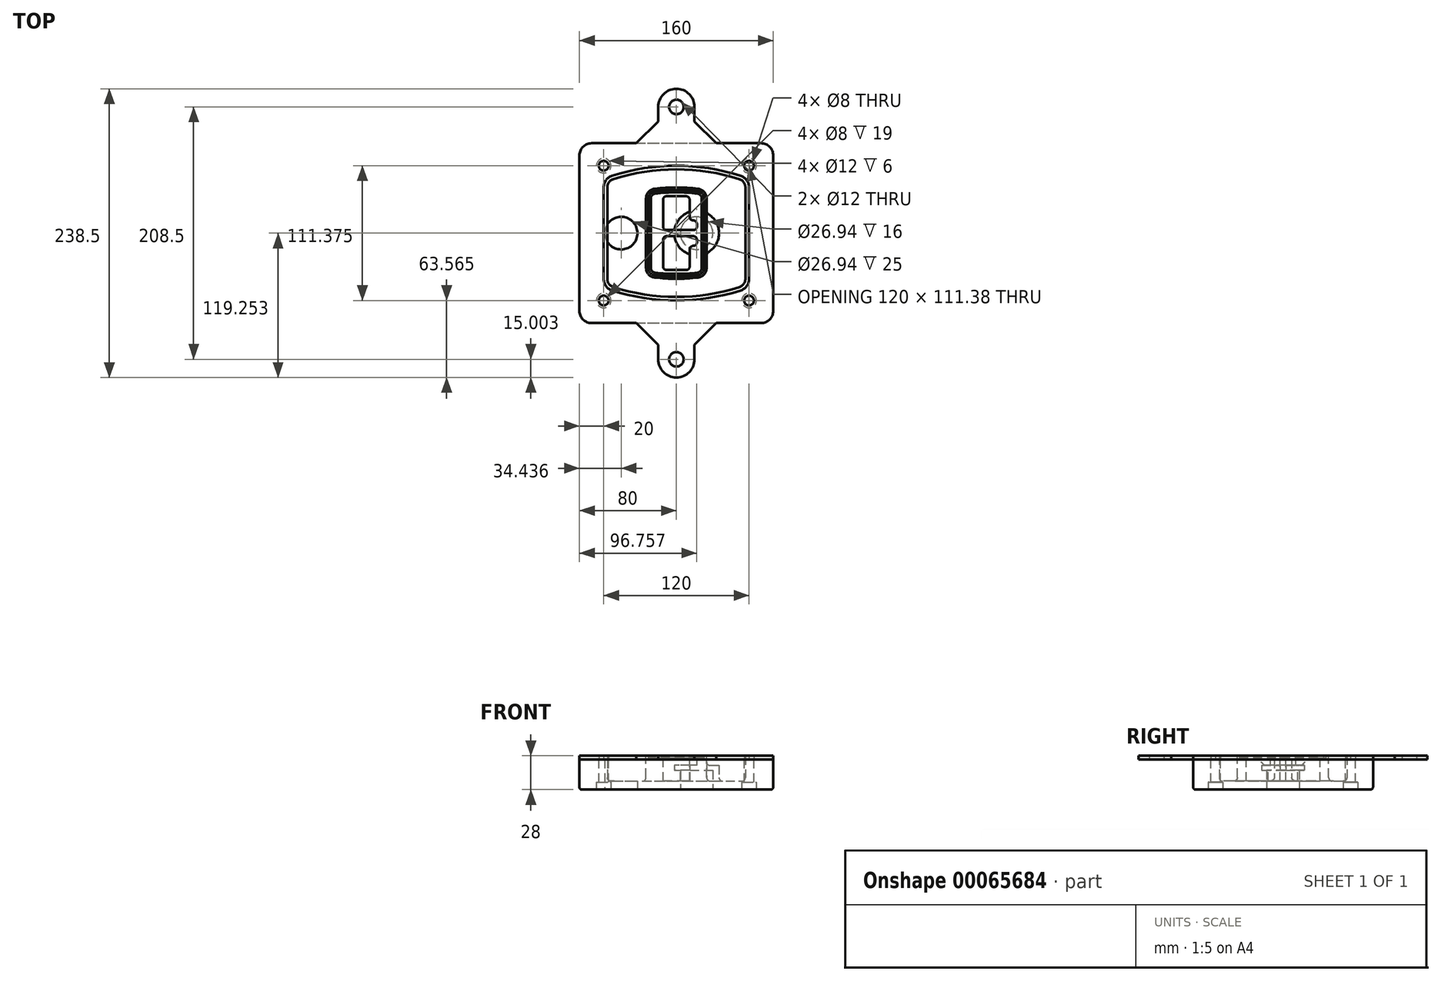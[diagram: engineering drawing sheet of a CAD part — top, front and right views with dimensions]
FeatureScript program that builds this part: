
annotation { "Feature Type Name" : "Feature", "Feature Type Description" : "" }
export const myFeature = defineFeature(function(context is Context, id is Id, definition is map)
    precondition{}
    {
        {
            var Q0;
            Q0=qCreatedBy(makeId("Top.planeOp"),FACE);
            var sketch = newSketch(context, id + "F0", { "sketchPlane" : qUnion([Q0])});
            skPoint(sketch, "E0.rect.middle", {"position": v(0, 0) * mm});
            skLineSegment(sketch, "E1.bottom", {"start": v(24.05, 28.38) * mm, "end": v(164.05, 28.38) * mm});
            skLineSegment(sketch, "E1.top", {"start": v(24.05, 176.88) * mm, "end": v(164.05, 176.88) * mm});
            skLineSegment(sketch, "E1.left", {"start": v(14.05, 38.38) * mm, "end": v(14.05, 166.88) * mm});
            skLineSegment(sketch, "E1.right", {"start": v(174.05, 38.38) * mm, "end": v(174.05, 166.88) * mm});
            skLineSegment(sketch, "E2", {"start": v(14.05, 176.88) * mm, "end": v(174.05, 28.38) * mm, "construction": true});
            skLineSegment(sketch, "E3", {"start": v(174.05, 176.88) * mm, "end": v(14.05, 28.38) * mm, "construction": true});
            skCircle(sketch, "E4", {"center": v(34.05, 158.32) * mm, "radius": 4 * mm});
            skCircle(sketch, "E5", {"center": v(154.05, 158.32) * mm, "radius": 4 * mm});
            skCircle(sketch, "E6", {"center": v(154.05, 46.95) * mm, "radius": 4 * mm});
            skCircle(sketch, "E7", {"center": v(34.05, 46.95) * mm, "radius": 4 * mm});
            skLineSegment(sketch, "E8", {"start": v(34.05, 158.32) * mm, "end": v(154.05, 158.32) * mm, "construction": true});
            skLineSegment(sketch, "E9", {"start": v(154.05, 158.32) * mm, "end": v(154.05, 46.95) * mm, "construction": true});
            skLineSegment(sketch, "E10", {"start": v(154.05, 46.95) * mm, "end": v(34.05, 46.95) * mm, "construction": true});
            skLineSegment(sketch, "E11", {"start": v(34.05, 46.95) * mm, "end": v(34.05, 158.32) * mm, "construction": true});
            skLineSegment(sketch, "E12", {"start": v(34.05, 140.5) * mm, "end": v(34.05, 64.76) * mm});
            skLineSegment(sketch, "E13", {"start": v(154.05, 140.5) * mm, "end": v(154.05, 64.76) * mm});
            skArc(sketch, "E14", {"start": v(147.1, 150.02) * mm, "mid": v(94.05, 158.32) * mm, "end": v(41, 150.02) * mm});
            skArc(sketch, "E15", {"start": v(41, 55.24) * mm, "mid": v(94.05, 46.95) * mm, "end": v(147.1, 55.24) * mm});
            skLineSegment(sketch, "E16", {"start": v(34.05, 102.63) * mm, "end": v(154.05, 102.63) * mm, "construction": true});
            skPoint(sketch, "E17.visualSharp", {"position": v(34.05, 57.63) * mm});
            skArc(sketch, "E17.filletArc", {"start": v(34.05, 64.76) * mm, "mid": v(35.97, 58.87) * mm, "end": v(41, 55.24) * mm});
            skPoint(sketch, "E18.visualSharp", {"position": v(34.05, 147.63) * mm});
            skArc(sketch, "E18.filletArc", {"start": v(41, 150.02) * mm, "mid": v(35.97, 146.4) * mm, "end": v(34.05, 140.5) * mm});
            skPoint(sketch, "E19.visualSharp", {"position": v(154.05, 147.63) * mm});
            skArc(sketch, "E19.filletArc", {"start": v(154.05, 140.5) * mm, "mid": v(152.13, 146.4) * mm, "end": v(147.1, 150.02) * mm});
            skPoint(sketch, "E20.visualSharp", {"position": v(154.05, 57.63) * mm});
            skArc(sketch, "E20.filletArc", {"start": v(147.1, 55.24) * mm, "mid": v(152.13, 58.87) * mm, "end": v(154.05, 64.76) * mm});
            skPoint(sketch, "E21.visualSharp", {"position": v(14.05, 176.88) * mm});
            skArc(sketch, "E21.filletArc", {"start": v(24.05, 176.88) * mm, "mid": v(16.98, 173.95) * mm, "end": v(14.05, 166.88) * mm});
            skPoint(sketch, "E22.visualSharp", {"position": v(174.05, 176.88) * mm});
            skArc(sketch, "E22.filletArc", {"start": v(174.05, 166.88) * mm, "mid": v(171.12, 173.95) * mm, "end": v(164.05, 176.88) * mm});
            skPoint(sketch, "E23.visualSharp", {"position": v(174.05, 28.38) * mm});
            skArc(sketch, "E23.filletArc", {"start": v(164.05, 28.38) * mm, "mid": v(171.12, 31.31) * mm, "end": v(174.05, 38.38) * mm});
            skPoint(sketch, "E24.visualSharp", {"position": v(14.05, 28.38) * mm});
            skArc(sketch, "E24.filletArc", {"start": v(14.05, 38.38) * mm, "mid": v(16.98, 31.31) * mm, "end": v(24.05, 28.38) * mm});
            skArc(sketch, "E25.0", {"start": v(151.05, 140.5) * mm, "mid": v(149.7, 144.63) * mm, "end": v(146.19, 147.17) * mm});
            skLineSegment(sketch, "E25.1", {"start": v(151.05, 140.5) * mm, "end": v(151.05, 64.76) * mm});
            skArc(sketch, "E25.2", {"start": v(146.19, 58.1) * mm, "mid": v(149.7, 60.64) * mm, "end": v(151.05, 64.76) * mm});
            skArc(sketch, "E25.3", {"start": v(41.91, 58.1) * mm, "mid": v(94.05, 49.95) * mm, "end": v(146.19, 58.1) * mm});
            skArc(sketch, "E25.4", {"start": v(37.05, 64.76) * mm, "mid": v(38.4, 60.64) * mm, "end": v(41.91, 58.1) * mm});
            skArc(sketch, "E25.5", {"start": v(146.19, 147.17) * mm, "mid": v(94.05, 155.32) * mm, "end": v(41.91, 147.17) * mm});
            skLineSegment(sketch, "E25.6", {"start": v(37.05, 140.5) * mm, "end": v(37.05, 64.76) * mm});
            skArc(sketch, "E25.7", {"start": v(41.91, 147.17) * mm, "mid": v(38.4, 144.63) * mm, "end": v(37.05, 140.5) * mm});
            skArc(sketch, "E26.0", {"start": v(39.78, 153.83) * mm, "mid": v(32.74, 148.75) * mm, "end": v(30.05, 140.5) * mm});
            skArc(sketch, "E26.1", {"start": v(148.32, 153.83) * mm, "mid": v(94.05, 162.32) * mm, "end": v(39.78, 153.83) * mm});
            skArc(sketch, "E26.2", {"start": v(158.05, 140.5) * mm, "mid": v(155.36, 148.75) * mm, "end": v(148.32, 153.83) * mm});
            skLineSegment(sketch, "E26.3", {"start": v(158.05, 140.5) * mm, "end": v(158.05, 64.76) * mm});
            skArc(sketch, "E26.4", {"start": v(148.32, 51.43) * mm, "mid": v(155.36, 56.51) * mm, "end": v(158.05, 64.76) * mm});
            skLineSegment(sketch, "E26.5", {"start": v(30.05, 140.5) * mm, "end": v(30.05, 64.76) * mm});
            skArc(sketch, "E26.6", {"start": v(39.78, 51.43) * mm, "mid": v(94.05, 42.95) * mm, "end": v(148.32, 51.43) * mm});
            skArc(sketch, "E26.7", {"start": v(30.05, 64.76) * mm, "mid": v(32.74, 56.51) * mm, "end": v(39.78, 51.43) * mm});
            skSolve(sketch);
        }
        {
            var Q0;
            Q0=makeQuery(id+"F0.imprint","IMPRINT",FACE,{"disambiguationData":[TD([[makeQuery(id+"F0.imprint","IMPRINT",EDGE,{"derivedFrom":sQuery(id+"F0.wireOp",EDGE,"E1.bottom")}),1.0]])]});
            var Q1;
            Q1=makeQuery(id+"F0.imprint","IMPRINT",FACE,{"disambiguationData":[TD([[makeQuery(id+"F0.imprint","IMPRINT",EDGE,{"derivedFrom":sQuery(id+"F0.wireOp",EDGE,"E12")}),1.0]])]});
            var Q2;
            Q2=makeQuery(id+"F0.imprint","IMPRINT",FACE,{"disambiguationData":[TD([[makeQuery(id+"F0.imprint","IMPRINT",EDGE,{"derivedFrom":sQuery(id+"F0.wireOp",EDGE,"E25.0")}),1.0]])]});
            var Q3;
            Q3=makeQuery(id+"F0.imprint","IMPRINT",FACE,{"disambiguationData":[TD([[makeQuery(id+"F0.imprint","IMPRINT",EDGE,{"derivedFrom":sQuery(id+"F0.wireOp",EDGE,"E12")}),-1.0]])]});
            extrude(context, id + "F1", {"entities" : qUnion([Q0, Q1, Q2, Q3]), "oppositeDirection" : true, "depth" : 25 * mm});
        }
        {
            var Q0;
            Q0=makeQuery(id+"F0.imprint","IMPRINT",FACE,{"disambiguationData":[TD([[makeQuery(id+"F0.imprint","IMPRINT",EDGE,{"derivedFrom":sQuery(id+"F0.wireOp",EDGE,"E12")}),1.0]])]});
            extrude(context, id + "F2", {"entities" : qUnion([Q0]), "operationType" : NewBodyOperationType.ADD, "depth" : 3 * mm});
        }
        {
            var Q0;
            Q0=makeQuery(id+"F0.imprint","IMPRINT",FACE,{"disambiguationData":[TD([[makeQuery(id+"F0.imprint","IMPRINT",EDGE,{"derivedFrom":sQuery(id+"F0.wireOp",EDGE,"E25.0")}),1.0]])]});
            extrude(context, id + "F3", {"entities" : qUnion([Q0]), "operationType" : NewBodyOperationType.REMOVE, "oppositeDirection" : true, "depth" : 18 * mm});
        }
        {
            var Q0;
            Q0=makeQuery(id+"F2.opExtrude","CAP_FACE",FACE,{"disambiguationData":[OSD([sQuery(id+"F0.wireOp",EDGE,"E12"),sQuery(id+"F0.wireOp",EDGE,"E13"),sQuery(id+"F0.wireOp",EDGE,"E14"),sQuery(id+"F0.wireOp",EDGE,"E15"),sQuery(id+"F0.wireOp",EDGE,"E17.filletArc"),sQuery(id+"F0.wireOp",EDGE,"E18.filletArc"),sQuery(id+"F0.wireOp",EDGE,"E19.filletArc"),sQuery(id+"F0.wireOp",EDGE,"E20.filletArc"),sQuery(id+"F0.wireOp",EDGE,"E25.0"),sQuery(id+"F0.wireOp",EDGE,"E25.1"),sQuery(id+"F0.wireOp",EDGE,"E25.2"),sQuery(id+"F0.wireOp",EDGE,"E25.3"),sQuery(id+"F0.wireOp",EDGE,"E25.4"),sQuery(id+"F0.wireOp",EDGE,"E25.5"),sQuery(id+"F0.wireOp",EDGE,"E25.6"),sQuery(id+"F0.wireOp",EDGE,"E25.7")])],"isStart":false});
            var sketch = newSketch(context, id + "F4", { "sketchPlane" : qUnion([Q0])});
            skArc(sketch, "E27.0", {"start": v(76.13, 65.98) * mm, "mid": v(94.05, 64.95) * mm, "end": v(111.97, 65.98) * mm});
            skArc(sketch, "E28.0", {"start": v(111.97, 139.29) * mm, "mid": v(94.05, 140.32) * mm, "end": v(76.13, 139.29) * mm});
            skLineSegment(sketch, "E29", {"start": v(69.05, 131.34) * mm, "end": v(69.05, 73.93) * mm});
            skLineSegment(sketch, "E30", {"start": v(119.05, 131.34) * mm, "end": v(119.05, 73.93) * mm});
            skLineSegment(sketch, "E31", {"start": v(69.05, 138.3) * mm, "end": v(119.05, 138.3) * mm, "construction": true});
            skLineSegment(sketch, "E32", {"start": v(69.05, 66.96) * mm, "end": v(119.05, 66.96) * mm, "construction": true});
            skPoint(sketch, "E33.visualSharp", {"position": v(69.05, 138.3) * mm});
            skArc(sketch, "E33.filletArc", {"start": v(76.13, 139.29) * mm, "mid": v(71.08, 136.66) * mm, "end": v(69.05, 131.34) * mm});
            skPoint(sketch, "E34.visualSharp", {"position": v(119.05, 138.3) * mm});
            skArc(sketch, "E34.filletArc", {"start": v(119.05, 131.34) * mm, "mid": v(117.02, 136.66) * mm, "end": v(111.97, 139.29) * mm});
            skPoint(sketch, "E35.visualSharp", {"position": v(119.05, 66.96) * mm});
            skArc(sketch, "E35.filletArc", {"start": v(111.97, 65.98) * mm, "mid": v(117.02, 68.6) * mm, "end": v(119.05, 73.93) * mm});
            skPoint(sketch, "E36.visualSharp", {"position": v(69.05, 66.96) * mm});
            skArc(sketch, "E36.filletArc", {"start": v(69.05, 73.93) * mm, "mid": v(71.08, 68.6) * mm, "end": v(76.13, 65.98) * mm});
            skArc(sketch, "E37.0", {"start": v(146.19, 147.17) * mm, "mid": v(94.05, 155.32) * mm, "end": v(41.91, 147.17) * mm});
            skArc(sketch, "E37.1", {"start": v(41.91, 147.17) * mm, "mid": v(38.4, 144.63) * mm, "end": v(37.05, 140.5) * mm});
            skLineSegment(sketch, "E37.2", {"start": v(37.05, 140.5) * mm, "end": v(37.05, 64.76) * mm});
            skArc(sketch, "E37.3", {"start": v(37.05, 64.76) * mm, "mid": v(38.4, 60.64) * mm, "end": v(41.91, 58.1) * mm});
            skArc(sketch, "E37.4", {"start": v(41.91, 58.1) * mm, "mid": v(94.05, 49.95) * mm, "end": v(146.19, 58.1) * mm});
            skArc(sketch, "E37.5", {"start": v(146.19, 58.1) * mm, "mid": v(149.7, 60.64) * mm, "end": v(151.05, 64.76) * mm});
            skLineSegment(sketch, "E37.6", {"start": v(151.05, 140.5) * mm, "end": v(151.05, 64.76) * mm});
            skArc(sketch, "E37.7", {"start": v(151.05, 140.5) * mm, "mid": v(149.7, 144.63) * mm, "end": v(146.19, 147.17) * mm});
            skLineSegment(sketch, "E38.0", {"start": v(117.05, 131.34) * mm, "end": v(117.05, 73.93) * mm});
            skArc(sketch, "E38.1", {"start": v(111.74, 67.97) * mm, "mid": v(115.53, 69.94) * mm, "end": v(117.05, 73.93) * mm});
            skArc(sketch, "E38.2", {"start": v(76.36, 67.97) * mm, "mid": v(94.05, 66.95) * mm, "end": v(111.74, 67.97) * mm});
            skArc(sketch, "E38.3", {"start": v(71.05, 73.93) * mm, "mid": v(72.57, 69.94) * mm, "end": v(76.36, 67.97) * mm});
            skLineSegment(sketch, "E38.4", {"start": v(71.05, 131.34) * mm, "end": v(71.05, 73.93) * mm});
            skArc(sketch, "E38.5", {"start": v(117.05, 131.34) * mm, "mid": v(115.53, 135.33) * mm, "end": v(111.74, 137.3) * mm});
            skArc(sketch, "E38.6", {"start": v(76.36, 137.3) * mm, "mid": v(72.57, 135.33) * mm, "end": v(71.05, 131.34) * mm});
            skArc(sketch, "E38.7", {"start": v(111.74, 137.3) * mm, "mid": v(94.05, 138.32) * mm, "end": v(76.36, 137.3) * mm});
            skArc(sketch, "E39.0", {"start": v(115.05, 131.34) * mm, "mid": v(114.04, 134) * mm, "end": v(111.51, 135.31) * mm});
            skLineSegment(sketch, "E39.1", {"start": v(115.05, 131.34) * mm, "end": v(115.05, 73.93) * mm});
            skArc(sketch, "E39.2", {"start": v(111.51, 69.95) * mm, "mid": v(114.04, 71.27) * mm, "end": v(115.05, 73.93) * mm});
            skArc(sketch, "E39.3", {"start": v(76.59, 69.95) * mm, "mid": v(94.05, 68.95) * mm, "end": v(111.51, 69.95) * mm});
            skArc(sketch, "E39.4", {"start": v(73.05, 73.93) * mm, "mid": v(74.06, 71.27) * mm, "end": v(76.59, 69.95) * mm});
            skArc(sketch, "E39.5", {"start": v(111.51, 135.31) * mm, "mid": v(94.05, 136.32) * mm, "end": v(76.59, 135.31) * mm});
            skLineSegment(sketch, "E39.6", {"start": v(73.05, 131.34) * mm, "end": v(73.05, 73.93) * mm});
            skArc(sketch, "E39.7", {"start": v(76.59, 135.31) * mm, "mid": v(74.06, 134) * mm, "end": v(73.05, 131.34) * mm});
            skLineSegment(sketch, "E40", {"start": v(69.05, 102.63) * mm, "end": v(119.05, 102.63) * mm, "construction": true});
            skLineSegment(sketch, "E41", {"start": v(83.05, 108.13) * mm, "end": v(83.05, 130.13) * mm});
            skLineSegment(sketch, "E42", {"start": v(86.05, 133.13) * mm, "end": v(102.05, 133.13) * mm});
            skLineSegment(sketch, "E43", {"start": v(105.05, 130.13) * mm, "end": v(105.05, 116.13) * mm});
            skLineSegment(sketch, "E44", {"start": v(108.05, 113.13) * mm, "end": v(108.05, 113.13) * mm});
            skLineSegment(sketch, "E45", {"start": v(111.05, 110.13) * mm, "end": v(111.05, 108.13) * mm});
            skLineSegment(sketch, "E46", {"start": v(108.05, 105.13) * mm, "end": v(86.05, 105.13) * mm});
            skPoint(sketch, "E47.visualSharp", {"position": v(83.05, 133.13) * mm});
            skArc(sketch, "E47.filletArc", {"start": v(86.05, 133.13) * mm, "mid": v(83.93, 132.25) * mm, "end": v(83.05, 130.13) * mm});
            skPoint(sketch, "E48.visualSharp", {"position": v(105.05, 133.13) * mm});
            skArc(sketch, "E48.filletArc", {"start": v(105.05, 130.13) * mm, "mid": v(104.17, 132.25) * mm, "end": v(102.05, 133.13) * mm});
            skPoint(sketch, "E49.visualSharp", {"position": v(105.05, 113.13) * mm});
            skArc(sketch, "E49.filletArc", {"start": v(105.05, 116.13) * mm, "mid": v(105.93, 114.01) * mm, "end": v(108.05, 113.13) * mm});
            skPoint(sketch, "E50.visualSharp", {"position": v(111.05, 113.13) * mm});
            skArc(sketch, "E50.filletArc", {"start": v(111.05, 110.13) * mm, "mid": v(110.17, 112.25) * mm, "end": v(108.05, 113.13) * mm});
            skPoint(sketch, "E51.visualSharp", {"position": v(111.05, 105.13) * mm});
            skArc(sketch, "E51.filletArc", {"start": v(108.05, 105.13) * mm, "mid": v(110.17, 106.01) * mm, "end": v(111.05, 108.13) * mm});
            skPoint(sketch, "E52.visualSharp", {"position": v(83.05, 105.13) * mm});
            skArc(sketch, "E52.filletArc", {"start": v(83.05, 108.13) * mm, "mid": v(83.93, 106.01) * mm, "end": v(86.05, 105.13) * mm});
            skLineSegment(sketch, "E53.0.MirrorCS", {"start": v(108.05, 100.13) * mm, "end": v(86.05, 100.13) * mm});
            skArc(sketch, "E54.0.MirrorCS", {"start": v(83.05, 97.13) * mm, "mid": v(83.93, 99.25) * mm, "end": v(86.05, 100.13) * mm});
            skLineSegment(sketch, "E55.0.MirrorCS", {"start": v(83.05, 97.13) * mm, "end": v(83.05, 75.13) * mm});
            skArc(sketch, "E56.0.MirrorCS", {"start": v(86.05, 72.13) * mm, "mid": v(83.93, 73.01) * mm, "end": v(83.05, 75.13) * mm});
            skLineSegment(sketch, "E57.0.MirrorCS", {"start": v(86.05, 72.13) * mm, "end": v(102.05, 72.13) * mm});
            skArc(sketch, "E58.0.MirrorCS", {"start": v(105.05, 75.13) * mm, "mid": v(104.17, 73.01) * mm, "end": v(102.05, 72.13) * mm});
            skLineSegment(sketch, "E59.0.MirrorCS", {"start": v(105.05, 75.13) * mm, "end": v(105.05, 89.13) * mm});
            skArc(sketch, "E60.0.MirrorCS", {"start": v(105.05, 89.13) * mm, "mid": v(105.93, 91.25) * mm, "end": v(108.05, 92.13) * mm});
            skArc(sketch, "E61.0.MirrorCS", {"start": v(111.05, 95.13) * mm, "mid": v(110.17, 93.01) * mm, "end": v(108.05, 92.13) * mm});
            skLineSegment(sketch, "E62.0.MirrorCS", {"start": v(111.05, 95.13) * mm, "end": v(111.05, 97.13) * mm});
            skArc(sketch, "E63.0.MirrorCS", {"start": v(108.05, 100.13) * mm, "mid": v(110.17, 99.25) * mm, "end": v(111.05, 97.13) * mm});
            skSolve(sketch);
        }
        {
            var Q0;
            Q0=makeQuery(id+"F4.imprint","IMPRINT",FACE,{"disambiguationData":[TD([[makeQuery(id+"F4.imprint","IMPRINT",EDGE,{"derivedFrom":sQuery(id+"F4.wireOp",EDGE,"E27.0")}),1.0]])]});
            var Q1;
            Q1=makeQuery(id+"F4.imprint","IMPRINT",FACE,{"disambiguationData":[TD([[makeQuery(id+"F4.imprint","IMPRINT",EDGE,{"derivedFrom":sQuery(id+"F4.wireOp",EDGE,"E38.0")}),-1.0]])]});
            var Q2;
            Q2=makeQuery(id+"F4.imprint","IMPRINT",FACE,{"disambiguationData":[TD([[makeQuery(id+"F4.imprint","IMPRINT",EDGE,{"derivedFrom":sQuery(id+"F4.wireOp",EDGE,"E39.0")}),1.0]])]});
            extrude(context, id + "F5", {"entities" : qUnion([Q0, Q1, Q2]), "operationType" : NewBodyOperationType.ADD, "endBound" : BoundingType.UP_TO_NEXT, "oppositeDirection" : true, "depth" : 25 * mm});
        }
        {
            var Q0;
            Q0=makeQuery(id+"F4.imprint","IMPRINT",FACE,{"disambiguationData":[TD([[makeQuery(id+"F4.imprint","IMPRINT",EDGE,{"derivedFrom":sQuery(id+"F4.wireOp",EDGE,"E38.0")}),-1.0]])]});
            extrude(context, id + "F6", {"entities" : qUnion([Q0]), "operationType" : NewBodyOperationType.REMOVE, "oppositeDirection" : true, "depth" : 2 * mm});
        }
        {
            var Q0;
            Q0=makeQuery(id+"F1.opExtrude","CAP_FACE",FACE,{"disambiguationData":[OSD([sQuery(id+"F0.wireOp",EDGE,"E1.bottom"),sQuery(id+"F0.wireOp",EDGE,"E1.top"),sQuery(id+"F0.wireOp",EDGE,"E1.left"),sQuery(id+"F0.wireOp",EDGE,"E1.right"),sQuery(id+"F0.wireOp",EDGE,"E4"),sQuery(id+"F0.wireOp",EDGE,"E5"),sQuery(id+"F0.wireOp",EDGE,"E6"),sQuery(id+"F0.wireOp",EDGE,"E7"),sQuery(id+"F0.wireOp",EDGE,"E21.filletArc"),sQuery(id+"F0.wireOp",EDGE,"E22.filletArc"),sQuery(id+"F0.wireOp",EDGE,"E23.filletArc"),sQuery(id+"F0.wireOp",EDGE,"E24.filletArc")])],"isStart":false});
            var sketch = newSketch(context, id + "F7", { "sketchPlane" : qUnion([Q0])});
            skCircle(sketch, "E64", {"center": v(110.8, -102.63) * mm, "radius": 13.47 * mm});
            skCircle(sketch, "E65", {"center": v(48.49, -102.63) * mm, "radius": 13.47 * mm});
            skLineSegment(sketch, "E66", {"start": v(174.05, -102.63) * mm, "end": v(14.05, -102.63) * mm});
            skCircle(sketch, "E67", {"center": v(110.8, -102.63) * mm, "radius": 18.47 * mm});
            skCircle(sketch, "E68", {"center": v(154.05, -158.32) * mm, "radius": 6 * mm});
            skCircle(sketch, "E69", {"center": v(34.05, -158.32) * mm, "radius": 6 * mm});
            skCircle(sketch, "E70", {"center": v(34.05, -46.95) * mm, "radius": 6 * mm});
            skCircle(sketch, "E71", {"center": v(154.05, -46.95) * mm, "radius": 6 * mm});
            skSolve(sketch);
        }
        {
            var Q0;
            {var subQ1=sQuery(id+"F7.wireOp",EDGE,"E66");var subQ4=sQuery(id+"F7.wireOp",EDGE,"E64");var subQ6=makeQuery(id+"F7.imprint","INTERSECT",VERTEX,{"disambiguationData":[OD(0.0)],"derivedFrom":[subQ4,subQ1]});Q0=makeQuery(id+"F7.imprint","IMPRINT",FACE,{"disambiguationData":[TD([[makeQuery(id+"F7.imprint","IMPRINT",EDGE,{"disambiguationData":[TD([[subQ6,-1.0]])],"derivedFrom":subQ4}),-1.0]])]});}
            var Q1;
            {var subQ0=sQuery(id+"F7.wireOp",EDGE,"E66");var subQ1=sQuery(id+"F7.wireOp",EDGE,"E64");var subQ3=makeQuery(id+"F7.imprint","INTERSECT",VERTEX,{"disambiguationData":[OD(0.0)],"derivedFrom":[subQ1,subQ0]});Q1=makeQuery(id+"F7.imprint","IMPRINT",FACE,{"disambiguationData":[TD([[makeQuery(id+"F7.imprint","IMPRINT",EDGE,{"disambiguationData":[TD([[subQ3,-1.0]])],"derivedFrom":subQ1}),1.0]])]});}
            var Q2;
            {var subQ0=sQuery(id+"F7.wireOp",EDGE,"E66");var subQ1=sQuery(id+"F7.wireOp",EDGE,"E64");var subQ3=makeQuery(id+"F7.imprint","INTERSECT",VERTEX,{"disambiguationData":[OD(0.0)],"derivedFrom":[subQ1,subQ0]});Q2=makeQuery(id+"F7.imprint","IMPRINT",FACE,{"disambiguationData":[TD([[makeQuery(id+"F7.imprint","IMPRINT",EDGE,{"disambiguationData":[TD([[subQ3,1.0]])],"derivedFrom":subQ1}),1.0]])]});}
            var Q3;
            {var subQ1=sQuery(id+"F7.wireOp",EDGE,"E66");var subQ4=sQuery(id+"F7.wireOp",EDGE,"E64");var subQ6=makeQuery(id+"F7.imprint","INTERSECT",VERTEX,{"disambiguationData":[OD(0.0)],"derivedFrom":[subQ4,subQ1]});Q3=makeQuery(id+"F7.imprint","IMPRINT",FACE,{"disambiguationData":[TD([[makeQuery(id+"F7.imprint","IMPRINT",EDGE,{"disambiguationData":[TD([[subQ6,1.0]])],"derivedFrom":subQ4}),-1.0]])]});}
            extrude(context, id + "F8", {"entities" : qUnion([Q0, Q1, Q2, Q3]), "operationType" : NewBodyOperationType.ADD, "oppositeDirection" : true, "depth" : 20 * mm});
        }
        {
            var Q0;
            {var subQ0=sQuery(id+"F7.wireOp",EDGE,"E66");var subQ1=sQuery(id+"F7.wireOp",EDGE,"E64");var subQ3=makeQuery(id+"F7.imprint","INTERSECT",VERTEX,{"disambiguationData":[OD(0.0)],"derivedFrom":[subQ1,subQ0]});Q0=makeQuery(id+"F7.imprint","IMPRINT",FACE,{"disambiguationData":[TD([[makeQuery(id+"F7.imprint","IMPRINT",EDGE,{"disambiguationData":[TD([[subQ3,-1.0]])],"derivedFrom":subQ1}),1.0]])]});}
            var Q1;
            {var subQ0=sQuery(id+"F7.wireOp",EDGE,"E66");var subQ1=sQuery(id+"F7.wireOp",EDGE,"E64");var subQ3=makeQuery(id+"F7.imprint","INTERSECT",VERTEX,{"disambiguationData":[OD(0.0)],"derivedFrom":[subQ1,subQ0]});Q1=makeQuery(id+"F7.imprint","IMPRINT",FACE,{"disambiguationData":[TD([[makeQuery(id+"F7.imprint","IMPRINT",EDGE,{"disambiguationData":[TD([[subQ3,1.0]])],"derivedFrom":subQ1}),1.0]])]});}
            extrude(context, id + "F9", {"entities" : qUnion([Q0, Q1]), "operationType" : NewBodyOperationType.REMOVE, "oppositeDirection" : true, "depth" : 16 * mm});
        }
        {
            var Q0;
            {var subQ0=sQuery(id+"F7.wireOp",EDGE,"E66");var subQ1=sQuery(id+"F7.wireOp",EDGE,"E65");var subQ3=makeQuery(id+"F7.imprint","INTERSECT",VERTEX,{"disambiguationData":[OD(0.0)],"derivedFrom":[subQ1,subQ0]});Q0=makeQuery(id+"F7.imprint","IMPRINT",FACE,{"disambiguationData":[TD([[makeQuery(id+"F7.imprint","IMPRINT",EDGE,{"disambiguationData":[TD([[subQ3,-1.0]])],"derivedFrom":subQ1}),1.0]])]});}
            var Q1;
            {var subQ0=sQuery(id+"F7.wireOp",EDGE,"E66");var subQ1=sQuery(id+"F7.wireOp",EDGE,"E65");var subQ3=makeQuery(id+"F7.imprint","INTERSECT",VERTEX,{"disambiguationData":[OD(0.0)],"derivedFrom":[subQ1,subQ0]});Q1=makeQuery(id+"F7.imprint","IMPRINT",FACE,{"disambiguationData":[TD([[makeQuery(id+"F7.imprint","IMPRINT",EDGE,{"disambiguationData":[TD([[subQ3,1.0]])],"derivedFrom":subQ1}),1.0]])]});}
            extrude(context, id + "F10", {"entities" : qUnion([Q0, Q1]), "operationType" : NewBodyOperationType.REMOVE, "oppositeDirection" : true, "depth" : 25 * mm});
        }
        {
            var Q0;
            Q0=makeQuery(id+"F7.imprint","IMPRINT",FACE,{"disambiguationData":[TD([[makeQuery(id+"F7.imprint","IMPRINT",EDGE,{"derivedFrom":sQuery(id+"F7.wireOp",EDGE,"E68")}),1.0]])]});
            var Q1;
            Q1=makeQuery(id+"F7.imprint","IMPRINT",FACE,{"disambiguationData":[TD([[makeQuery(id+"F7.imprint","IMPRINT",EDGE,{"derivedFrom":makeQuery(id+"F1.opExtrude","CAP_EDGE",EDGE,{"disambiguationData":[OSD([sQuery(id+"F0.wireOp",EDGE,"E5")])],"isStart":false})}),-1.0]])]});
            var Q2;
            Q2=makeQuery(id+"F7.imprint","IMPRINT",FACE,{"disambiguationData":[TD([[makeQuery(id+"F7.imprint","IMPRINT",EDGE,{"derivedFrom":sQuery(id+"F7.wireOp",EDGE,"E69")}),1.0]])]});
            var Q3;
            Q3=makeQuery(id+"F7.imprint","IMPRINT",FACE,{"disambiguationData":[TD([[makeQuery(id+"F7.imprint","IMPRINT",EDGE,{"derivedFrom":makeQuery(id+"F1.opExtrude","CAP_EDGE",EDGE,{"disambiguationData":[OSD([sQuery(id+"F0.wireOp",EDGE,"E4")])],"isStart":false})}),-1.0]])]});
            var Q4;
            Q4=makeQuery(id+"F7.imprint","IMPRINT",FACE,{"disambiguationData":[TD([[makeQuery(id+"F7.imprint","IMPRINT",EDGE,{"derivedFrom":sQuery(id+"F7.wireOp",EDGE,"E70")}),1.0]])]});
            var Q5;
            Q5=makeQuery(id+"F7.imprint","IMPRINT",FACE,{"disambiguationData":[TD([[makeQuery(id+"F7.imprint","IMPRINT",EDGE,{"derivedFrom":makeQuery(id+"F1.opExtrude","CAP_EDGE",EDGE,{"disambiguationData":[OSD([sQuery(id+"F0.wireOp",EDGE,"E7")])],"isStart":false})}),-1.0]])]});
            var Q6;
            Q6=makeQuery(id+"F7.imprint","IMPRINT",FACE,{"disambiguationData":[TD([[makeQuery(id+"F7.imprint","IMPRINT",EDGE,{"derivedFrom":sQuery(id+"F7.wireOp",EDGE,"E71")}),1.0]])]});
            var Q7;
            Q7=makeQuery(id+"F7.imprint","IMPRINT",FACE,{"disambiguationData":[TD([[makeQuery(id+"F7.imprint","IMPRINT",EDGE,{"derivedFrom":makeQuery(id+"F1.opExtrude","CAP_EDGE",EDGE,{"disambiguationData":[OSD([sQuery(id+"F0.wireOp",EDGE,"E6")])],"isStart":false})}),-1.0]])]});
            extrude(context, id + "F11", {"entities" : qUnion([Q0, Q1, Q2, Q3, Q4, Q5, Q6, Q7]), "operationType" : NewBodyOperationType.REMOVE, "oppositeDirection" : true, "depth" : 6 * mm});
        }
        {
            var Q0;
            Q0=makeQuery(id+"F9.boolean.opBoolean","COPY",FACE,{"derivedFrom":makeQuery(id+"F9.opExtrude","CAP_FACE",FACE,{"disambiguationData":[OSD([sQuery(id+"F7.wireOp",EDGE,"E64")])],"isStart":false})});
            var sketch = newSketch(context, id + "F12", { "sketchPlane" : qUnion([Q0])});
            skArc(sketch, "E72.0", {"start": v(105.05, -85.08) * mm, "mid": v(96.62, -90.8) * mm, "end": v(92.5, -100.13) * mm});
            skArc(sketch, "E72.1", {"start": v(92.5, -105.13) * mm, "mid": v(96.62, -114.46) * mm, "end": v(105.05, -120.18) * mm});
            skLineSegment(sketch, "E73", {"start": v(92.5, -105.13) * mm, "end": v(108.05, -105.13) * mm});
            skLineSegment(sketch, "E74.0", {"start": v(108.05, -100.13) * mm, "end": v(92.5, -100.13) * mm});
            skArc(sketch, "E74.1", {"start": v(108.05, -100.13) * mm, "mid": v(110.17, -99.25) * mm, "end": v(111.05, -97.13) * mm});
            skLineSegment(sketch, "E74.2", {"start": v(111.05, -95.13) * mm, "end": v(111.05, -97.13) * mm});
            skArc(sketch, "E74.3", {"start": v(111.05, -95.13) * mm, "mid": v(110.17, -93.01) * mm, "end": v(108.05, -92.13) * mm});
            skArc(sketch, "E74.4", {"start": v(105.05, -89.13) * mm, "mid": v(105.93, -91.25) * mm, "end": v(108.05, -92.13) * mm});
            skLineSegment(sketch, "E74.5", {"start": v(105.05, -85.08) * mm, "end": v(105.05, -89.13) * mm});
            skLineSegment(sketch, "E74.7", {"start": v(108.05, -105.13) * mm, "end": v(92.5, -105.13) * mm});
            skArc(sketch, "E74.8", {"start": v(108.05, -105.13) * mm, "mid": v(110.17, -106.01) * mm, "end": v(111.05, -108.13) * mm});
            skLineSegment(sketch, "E74.9", {"start": v(111.05, -110.13) * mm, "end": v(111.05, -108.13) * mm});
            skArc(sketch, "E74.10", {"start": v(111.05, -110.13) * mm, "mid": v(110.17, -112.25) * mm, "end": v(108.05, -113.13) * mm});
            skArc(sketch, "E74.11", {"start": v(105.05, -116.13) * mm, "mid": v(105.93, -114.01) * mm, "end": v(108.05, -113.13) * mm});
            skLineSegment(sketch, "E74.12", {"start": v(105.05, -120.18) * mm, "end": v(105.05, -116.13) * mm});
            skPoint(sketch, "E75.orphan", {"position": v(105.05, -130.13) * mm});
            skPoint(sketch, "E76.orphan", {"position": v(86.05, -105.13) * mm});
            skPoint(sketch, "E77.orphan", {"position": v(86.05, -100.13) * mm});
            skPoint(sketch, "E78.orphan", {"position": v(105.05, -75.13) * mm});
            skSolve(sketch);
        }
        {
            var Q0;
            {var subQ7=sQuery(id+"F12.wireOp",EDGE,"E72.0");var subQ14=sQuery(id+"F12.wireOp",EDGE,"E72.1");var subQ16=sQuery(id+"F12.wireOp",EDGE,"E74.1");var subQ18=sQuery(id+"F12.wireOp",EDGE,"E74.8");Q0=qUnion([makeQuery(id+"F12.imprint","IMPRINT",FACE,{"disambiguationData":[TD([[makeQuery(id+"F12.imprint","IMPRINT",EDGE,{"derivedFrom":subQ7}),1.0]])]}),makeQuery(id+"F12.imprint","IMPRINT",FACE,{"disambiguationData":[TD([[makeQuery(id+"F12.imprint","IMPRINT",EDGE,{"derivedFrom":subQ14}),1.0]])]}),makeQuery(id+"F12.imprint","IMPRINT",FACE,{"disambiguationData":[TD([[makeQuery(id+"F12.imprint","IMPRINT",EDGE,{"derivedFrom":subQ16}),1.0]])]}),makeQuery(id+"F12.imprint","IMPRINT",FACE,{"disambiguationData":[TD([[makeQuery(id+"F12.imprint","IMPRINT",EDGE,{"derivedFrom":subQ18}),-1.0]])]})]);}
            var Q1;
            Q1=makeQuery(id+"F5.boolean.opBoolean","SPLIT",FACE,{"disambiguationData":[TD([makeQuery(id+"F5.opExtrude","SWEPT_FACE",FACE,{"disambiguationData":[OSD([sQuery(id+"F4.wireOp",EDGE,"E41")])]})])],"derivedFrom":makeQuery(id+"F3.boolean.opBoolean","COPY",FACE,{"derivedFrom":makeQuery(id+"F3.opExtrude","CAP_FACE",FACE,{"disambiguationData":[OSD([sQuery(id+"F0.wireOp",EDGE,"E25.0"),sQuery(id+"F0.wireOp",EDGE,"E25.1"),sQuery(id+"F0.wireOp",EDGE,"E25.2"),sQuery(id+"F0.wireOp",EDGE,"E25.3"),sQuery(id+"F0.wireOp",EDGE,"E25.4"),sQuery(id+"F0.wireOp",EDGE,"E25.5"),sQuery(id+"F0.wireOp",EDGE,"E25.6"),sQuery(id+"F0.wireOp",EDGE,"E25.7")])],"isStart":false})})});
            extrude(context, id + "F13", {"entities" : qUnion([Q0]), "operationType" : NewBodyOperationType.REMOVE, "endBound" : BoundingType.UP_TO_SURFACE, "endBoundEntityFace" : qUnion([Q1]), "depth" : 25 * mm});
        }
        {
            var Q0;
            Q0=makeQuery(id+"F3.boolean.opBoolean","COPY",EDGE,{"derivedFrom":makeQuery(id+"F3.opExtrude","CAP_EDGE",EDGE,{"disambiguationData":[OSD([sQuery(id+"F0.wireOp",EDGE,"E25.6")])],"isStart":false})});
            var Q1;
            Q1=makeQuery(id+"F8.boolean.opBoolean","INTERSECT",EDGE,{"derivedFrom":[makeQuery(id+"F5.opExtrude","SWEPT_FACE",FACE,{"disambiguationData":[OSD([sQuery(id+"F4.wireOp",EDGE,"E30")])]}),makeQuery(id+"F8.opExtrude","CAP_FACE",FACE,{"disambiguationData":[OSD([sQuery(id+"F7.wireOp",EDGE,"E67")])],"isStart":false})]});
            var Q2;
            Q2=makeQuery(id+"F8.boolean.opBoolean","INTERSECT",EDGE,{"disambiguationData":[OD(1.0)],"derivedFrom":[makeQuery(id+"F5.opExtrude","SWEPT_FACE",FACE,{"disambiguationData":[OSD([sQuery(id+"F4.wireOp",EDGE,"E30")])]}),makeQuery(id+"F8.opExtrude","SWEPT_FACE",FACE,{"disambiguationData":[OSD([sQuery(id+"F7.wireOp",EDGE,"E67")])]})]});
            var Q3;
            {var subQ0=sQuery(id+"F4.wireOp",EDGE,"E30");Q3=makeQuery(id+"F8.boolean.opBoolean","SPLIT",EDGE,{"disambiguationData":[TD([makeQuery(id+"F5.opExtrude","SWEPT_FACE",FACE,{"disambiguationData":[OSD([sQuery(id+"F4.wireOp",EDGE,"E35.filletArc")])]})])],"derivedFrom":makeQuery(id+"F5.opExtrude","CAP_EDGE",EDGE,{"disambiguationData":[OSD([subQ0])],"isStart":false})});}
            var Q4;
            {var subQ0=sQuery(id+"F0.wireOp",EDGE,"E25.7");var subQ1=sQuery(id+"F0.wireOp",EDGE,"E25.1");var subQ2=sQuery(id+"F0.wireOp",EDGE,"E25.6");var subQ3=sQuery(id+"F0.wireOp",EDGE,"E25.5");var subQ4=sQuery(id+"F0.wireOp",EDGE,"E25.4");var subQ5=sQuery(id+"F0.wireOp",EDGE,"E25.0");var subQ6=sQuery(id+"F0.wireOp",EDGE,"E25.2");var subQ7=sQuery(id+"F0.wireOp",EDGE,"E25.3");Q4=makeQuery(id+"F8.boolean.opBoolean","INTERSECT",EDGE,{"derivedFrom":[makeQuery(id+"F5.boolean.opBoolean","SPLIT",FACE,{"disambiguationData":[TD([makeQuery(id+"F2.opExtrude","SWEPT_FACE",FACE,{"disambiguationData":[OSD([subQ5])]})])],"derivedFrom":makeQuery(id+"F3.boolean.opBoolean","COPY",FACE,{"derivedFrom":makeQuery(id+"F3.opExtrude","CAP_FACE",FACE,{"disambiguationData":[OSD([subQ5,subQ1,subQ6,subQ7,subQ4,subQ3,subQ2,subQ0])],"isStart":false})})}),makeQuery(id+"F8.opExtrude","SWEPT_FACE",FACE,{"disambiguationData":[OSD([sQuery(id+"F7.wireOp",EDGE,"E67")])]})]});}
            var Q5;
            Q5=makeQuery(id+"F8.boolean.opBoolean","INTERSECT",EDGE,{"disambiguationData":[OD(0.0)],"derivedFrom":[makeQuery(id+"F5.opExtrude","SWEPT_FACE",FACE,{"disambiguationData":[OSD([sQuery(id+"F4.wireOp",EDGE,"E30")])]}),makeQuery(id+"F8.opExtrude","SWEPT_FACE",FACE,{"disambiguationData":[OSD([sQuery(id+"F7.wireOp",EDGE,"E67")])]})]});
            fillet(context, id + "F14", {"entities" : qUnion([Q0, Q1, Q2, Q3, Q4, Q5]), "radius" : 3 * mm, "tangentPropagation" : true, "allowEdgeOverflow" : false});
        }
        {
            var Q0;
            Q0=makeQuery(id+"F1.opExtrude","CAP_EDGE",EDGE,{"disambiguationData":[OSD([sQuery(id+"F0.wireOp",EDGE,"E1.bottom")])],"isStart":false});
            fillet(context, id + "F15", {"entities" : qUnion([Q0]), "radius" : 2 * mm, "tangentPropagation" : true, "allowEdgeOverflow" : false});
        }
        {
            var Q0;
            {var subQ0=sQuery(id+"F0.wireOp",EDGE,"E22.filletArc");var subQ1=sQuery(id+"F0.wireOp",EDGE,"E7");var subQ2=sQuery(id+"F0.wireOp",EDGE,"E6");var subQ3=sQuery(id+"F0.wireOp",EDGE,"E5");var subQ4=sQuery(id+"F0.wireOp",EDGE,"E4");var subQ5=sQuery(id+"F0.wireOp",EDGE,"E1.bottom");var subQ6=sQuery(id+"F0.wireOp",EDGE,"E21.filletArc");var subQ7=sQuery(id+"F0.wireOp",EDGE,"E1.top");var subQ8=sQuery(id+"F0.wireOp",EDGE,"E1.left");var subQ9=sQuery(id+"F0.wireOp",EDGE,"E1.right");var subQ10=sQuery(id+"F0.wireOp",EDGE,"E23.filletArc");var subQ11=sQuery(id+"F0.wireOp",EDGE,"E24.filletArc");Q0=makeQuery(id+"F2.boolean.opBoolean","SPLIT",FACE,{"disambiguationData":[TD([makeQuery(id+"F1.opExtrude","SWEPT_FACE",FACE,{"disambiguationData":[OSD([subQ5])]})])],"derivedFrom":makeQuery(id+"F1.opExtrude","CAP_FACE",FACE,{"disambiguationData":[OSD([subQ5,subQ7,subQ8,subQ9,subQ4,subQ3,subQ2,subQ1,subQ6,subQ0,subQ10,subQ11])],"isStart":true})});}
            var sketch = newSketch(context, id + "F16", { "sketchPlane" : qUnion([Q0])});
            skLineSegment(sketch, "E79", {"start": v(94.05, 176.88) * mm, "end": v(94.05, 206.88) * mm, "construction": true});
            skCircle(sketch, "E80", {"center": v(94.05, 206.88) * mm, "radius": 6 * mm});
            skLineSegment(sketch, "E81", {"start": v(61.05, 176.88) * mm, "end": v(79.05, 194.88) * mm});
            skLineSegment(sketch, "E82", {"start": v(79.05, 194.88) * mm, "end": v(79.05, 206.88) * mm});
            skLineSegment(sketch, "E83", {"start": v(127.05, 176.88) * mm, "end": v(109.05, 194.88) * mm});
            skLineSegment(sketch, "E84", {"start": v(109.05, 194.88) * mm, "end": v(109.05, 206.88) * mm});
            skArc(sketch, "E85", {"start": v(109.05, 206.88) * mm, "mid": v(94.05, 221.88) * mm, "end": v(79.05, 206.88) * mm});
            skPoint(sketch, "E85.third.point", {"position": v(94.05, 221.88) * mm});
            skLineSegment(sketch, "E86.0", {"start": v(24.05, 176.88) * mm, "end": v(164.05, 176.88) * mm});
            skArc(sketch, "E87.0", {"start": v(24.05, 176.88) * mm, "mid": v(16.98, 173.95) * mm, "end": v(14.05, 166.88) * mm});
            skLineSegment(sketch, "E88.0", {"start": v(14.05, 38.38) * mm, "end": v(14.05, 166.88) * mm});
            skArc(sketch, "E89.0", {"start": v(14.05, 38.38) * mm, "mid": v(16.98, 31.31) * mm, "end": v(24.05, 28.38) * mm});
            skLineSegment(sketch, "E90.0", {"start": v(24.05, 28.38) * mm, "end": v(164.05, 28.38) * mm});
            skArc(sketch, "E91.0", {"start": v(164.05, 28.38) * mm, "mid": v(171.12, 31.31) * mm, "end": v(174.05, 38.38) * mm});
            skLineSegment(sketch, "E92.0", {"start": v(174.05, 38.38) * mm, "end": v(174.05, 166.88) * mm});
            skArc(sketch, "E93.0", {"start": v(174.05, 166.88) * mm, "mid": v(171.12, 173.95) * mm, "end": v(164.05, 176.88) * mm});
            skCircle(sketch, "E94.0", {"center": v(154.05, 158.32) * mm, "radius": 4 * mm});
            skCircle(sketch, "E95.0", {"center": v(34.05, 158.32) * mm, "radius": 4 * mm});
            skArc(sketch, "E96.0", {"start": v(147.1, 150.02) * mm, "mid": v(94.05, 158.32) * mm, "end": v(41, 150.02) * mm});
            skArc(sketch, "E97.0", {"start": v(41, 150.02) * mm, "mid": v(35.97, 146.4) * mm, "end": v(34.05, 140.5) * mm});
            skLineSegment(sketch, "E98.0", {"start": v(34.05, 140.5) * mm, "end": v(34.05, 64.76) * mm});
            skArc(sketch, "E99.0", {"start": v(34.05, 64.76) * mm, "mid": v(35.97, 58.87) * mm, "end": v(41, 55.24) * mm});
            skArc(sketch, "E100.0", {"start": v(41, 55.24) * mm, "mid": v(94.05, 46.95) * mm, "end": v(147.1, 55.24) * mm});
            skArc(sketch, "E101.0", {"start": v(147.1, 55.24) * mm, "mid": v(152.13, 58.87) * mm, "end": v(154.05, 64.76) * mm});
            skLineSegment(sketch, "E102.0", {"start": v(154.05, 140.5) * mm, "end": v(154.05, 64.76) * mm});
            skArc(sketch, "E103.0", {"start": v(154.05, 140.5) * mm, "mid": v(152.13, 146.4) * mm, "end": v(147.1, 150.02) * mm});
            skCircle(sketch, "E104.0", {"center": v(34.05, 46.95) * mm, "radius": 4 * mm});
            skCircle(sketch, "E105.0", {"center": v(154.05, 46.95) * mm, "radius": 4 * mm});
            skArc(sketch, "E106.MirrorCS", {"start": v(109.05, -1.62) * mm, "mid": v(94.05, -16.62) * mm, "end": v(79.05, -1.62) * mm});
            skLineSegment(sketch, "E107.MirrorCS", {"start": v(109.05, 10.38) * mm, "end": v(109.05, -1.62) * mm});
            skPoint(sketch, "E108.MirrorP", {"position": v(94.05, -16.62) * mm});
            skLineSegment(sketch, "E109.MirrorCS", {"start": v(94.05, 28.38) * mm, "end": v(94.05, -1.62) * mm, "construction": true});
            skCircle(sketch, "E110.MirrorC", {"center": v(94.05, -1.62) * mm, "radius": 6 * mm});
            skLineSegment(sketch, "E111.MirrorCS", {"start": v(61.05, 28.38) * mm, "end": v(79.05, 10.38) * mm});
            skLineSegment(sketch, "E112.MirrorCS", {"start": v(79.05, 10.38) * mm, "end": v(79.05, -1.62) * mm});
            skLineSegment(sketch, "E113.MirrorCS", {"start": v(127.05, 28.38) * mm, "end": v(109.05, 10.38) * mm});
            skSolve(sketch);
        }
        {
            var Q0;
            Q0 = qSketchRegion(id + "F16", true);
            var Q1;
            Q1=makeQuery(id+"F2.opExtrude","CAP_FACE",FACE,{"disambiguationData":[OSD([sQuery(id+"F0.wireOp",EDGE,"E12"),sQuery(id+"F0.wireOp",EDGE,"E13"),sQuery(id+"F0.wireOp",EDGE,"E14"),sQuery(id+"F0.wireOp",EDGE,"E15"),sQuery(id+"F0.wireOp",EDGE,"E17.filletArc"),sQuery(id+"F0.wireOp",EDGE,"E18.filletArc"),sQuery(id+"F0.wireOp",EDGE,"E19.filletArc"),sQuery(id+"F0.wireOp",EDGE,"E20.filletArc"),sQuery(id+"F0.wireOp",EDGE,"E25.0"),sQuery(id+"F0.wireOp",EDGE,"E25.1"),sQuery(id+"F0.wireOp",EDGE,"E25.2"),sQuery(id+"F0.wireOp",EDGE,"E25.3"),sQuery(id+"F0.wireOp",EDGE,"E25.4"),sQuery(id+"F0.wireOp",EDGE,"E25.5"),sQuery(id+"F0.wireOp",EDGE,"E25.6"),sQuery(id+"F0.wireOp",EDGE,"E25.7")])],"isStart":false});
            extrude(context, id + "F17", {"entities" : qUnion([Q0]), "endBound" : BoundingType.UP_TO_SURFACE, "endBoundEntityFace" : qUnion([Q1]), "depth" : 25 * mm});
        }
    });
